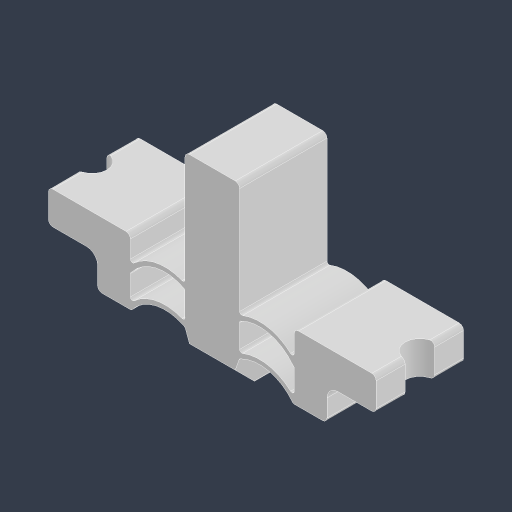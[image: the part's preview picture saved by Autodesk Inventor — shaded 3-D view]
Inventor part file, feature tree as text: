
AUTODESK INVENTOR PART (.ipt)
format: ipt  version: 2023.4 (Build 274418000, 418)  size: 246,272 bytes
history: native  units: mm
features: fillet x3, chamfer x2, sketch x2, extrude x1, hole x1
ambient origin geometry x8: Origin, YZ Plane, XZ Plane, XY Plane, X Axis, Y Axis, Z Axis, Center Point
bodies: Solid1 (feature_tree)
feature tree (9):
  extrude  "Extrusion1"  Depth=18.0mm
  hole  "Hole1"  [1 undecoded]
  chamfer  "Chamfer1"  Distance=3.0mm
  chamfer  "Chamfer2"  Distance=5.0mm
  fillet  "Fillet1"  Radius=3.0mm
  fillet  "Fillet2"  Radius=3.0mm
  fillet  "Fillet3"  Radius=9.0mm
  sketch  "Sketch1"  dims[d0=5.0mm d1=18.0mm]
  sketch  "Sketch2"  dims[d2=30.0mm d3=3.0mm d4=3.0mm d5=5.0mm d6=3.0mm d7=3.0mm d8=9.0mm d9=3.0mm d10=2.0mm d11=3.490659mm d12=0.4mm d13=4.0mm d14=3.0mm d15=8.0mm d16=0.0mm d17=0.0mm d18=2.7mm d19=6.0mm d20=5.5mm d21=2.9mm d22=90.0deg d23=8.0mm d24=20.594885mm d25=3.0mm d26=2.0mm d27=45.0deg d28=3.0mm d29=2.0mm d30=45.0deg d31=0.2mm d32=0.4mm d33=1.0mm]
note: 1 required parameter value undecoded (feature->parameter linkage not recoverable at this tier; creation-order binding heuristic only, values carry confidence <= 0.55)
